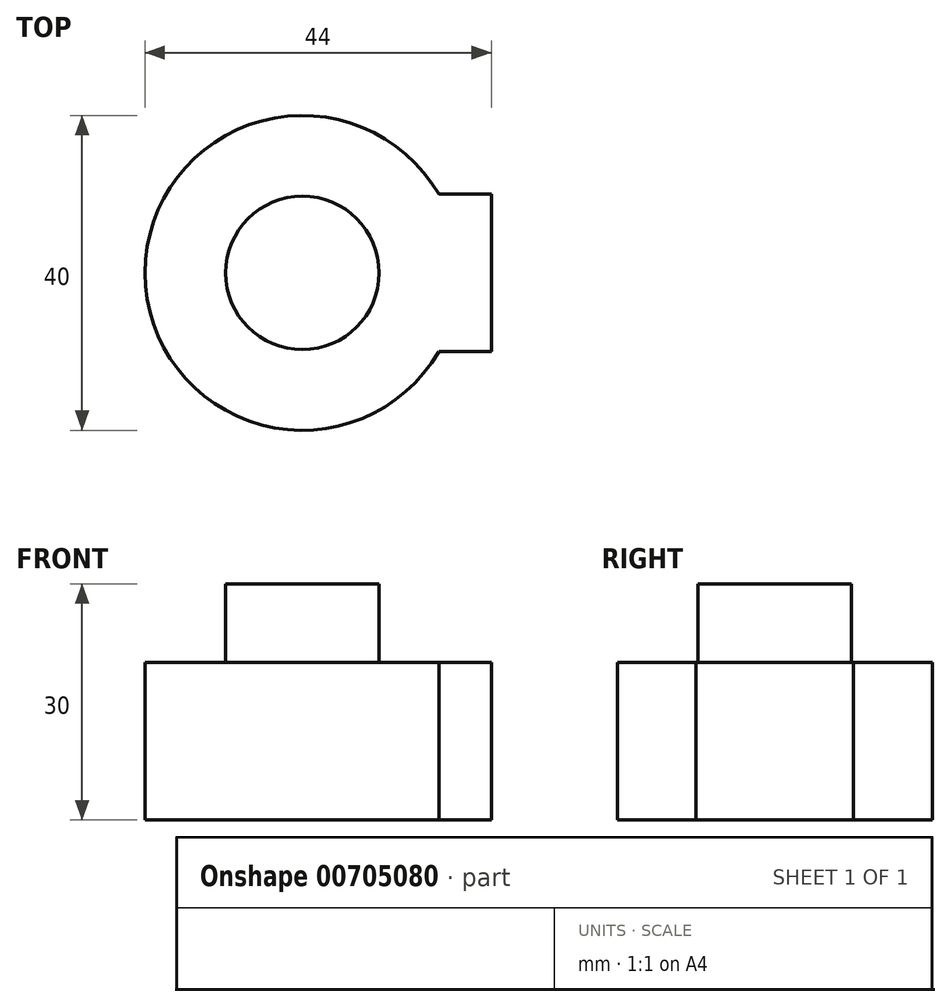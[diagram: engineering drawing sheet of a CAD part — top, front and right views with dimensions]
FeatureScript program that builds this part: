
annotation { "Feature Type Name" : "Feature", "Feature Type Description" : "" }
export const myFeature = defineFeature(function(context is Context, id is Id, definition is map)
    precondition{}
    {
        {
            var Q0;
            Q0=qCreatedBy(makeId("Top.planeOp"),FACE);
            var sketch = newSketch(context, id + "F0", { "sketchPlane" : qUnion([Q0])});
            skCircle(sketch, "E0", {"center": v(20, 20) * mm, "radius": 20 * mm});
            skLineSegment(sketch, "E1.bottom", {"start": v(44, 30) * mm, "end": v(20, 30) * mm});
            skLineSegment(sketch, "E1.top", {"start": v(44, 10) * mm, "end": v(20, 10) * mm});
            skLineSegment(sketch, "E1.left", {"start": v(44, 30) * mm, "end": v(44, 10) * mm});
            skLineSegment(sketch, "E1.right", {"start": v(20, 30) * mm, "end": v(20, 10) * mm});
            skSolve(sketch);
        }
        {
            var Q0;
            Q0 = qSketchRegion(id + "F0", true);
            extrude(context, id + "F1", {"entities" : qUnion([Q0]), "depth" : 20 * mm, "offsetDistance" : 25 * mm});
        }
        {
            var Q0;
            Q0=makeQuery(id+"F1.opExtrude","CAP_FACE",FACE,{"disambiguationData":[OSD([sQuery(id+"F0.wireOp",EDGE,"E0"),sQuery(id+"F0.wireOp",EDGE,"E1.bottom"),sQuery(id+"F0.wireOp",EDGE,"E1.top"),sQuery(id+"F0.wireOp",EDGE,"E1.left")])],"isStart":false});
            var sketch = newSketch(context, id + "F2", { "sketchPlane" : qUnion([Q0])});
            skCircle(sketch, "E2", {"center": v(20, 20) * mm, "radius": 9.75 * mm});
            skSolve(sketch);
        }
        {
            var Q0;
            Q0 = qSketchRegion(id + "F2", true);
            extrude(context, id + "F3", {"entities" : qUnion([Q0]), "operationType" : NewBodyOperationType.ADD, "depth" : 10 * mm, "offsetDistance" : 25 * mm});
        }
    });
